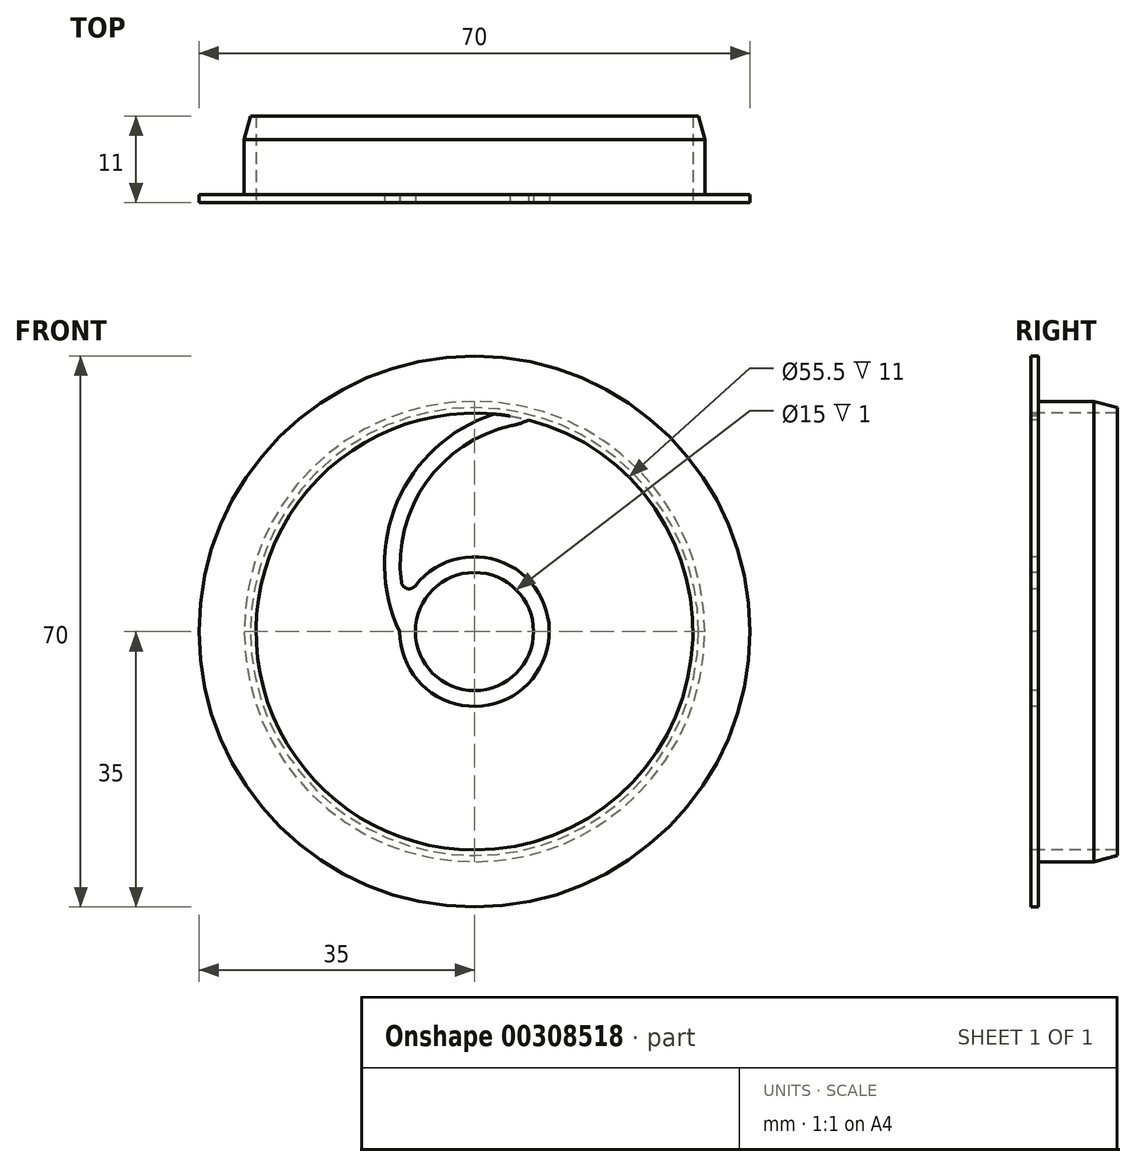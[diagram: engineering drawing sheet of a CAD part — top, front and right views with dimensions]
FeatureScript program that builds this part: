
annotation { "Feature Type Name" : "Feature", "Feature Type Description" : "" }
export const myFeature = defineFeature(function(context is Context, id is Id, definition is map)
    precondition{}
    {
        {
            var Q0;
            Q0=qCreatedBy(makeId("Front.planeOp"),FACE);
            var sketch = newSketch(context, id + "F0", { "sketchPlane" : qUnion([Q0])});
            skCircle(sketch, "E0", {"center": v(0, 0) * mm, "radius": 27.75 * mm});
            skCircle(sketch, "E1.0", {"center": v(0, 0) * mm, "radius": 29.25 * mm});
            skSolve(sketch);
        }
        {
            var Q0;
            Q0 = qSketchRegion(id + "F0", true);
            extrude(context, id + "F1", {"entities" : qUnion([Q0]), "oppositeDirection" : true, "depth" : 10 * mm});
        }
        {
            var Q0;
            Q0=makeQuery(id+"F1.opExtrude","CAP_FACE",FACE,{"disambiguationData":[OSD([sQuery(id+"F0.wireOp",EDGE,"E0"),sQuery(id+"F0.wireOp",EDGE,"E1.0")])],"isStart":true});
            var sketch = newSketch(context, id + "F2", { "sketchPlane" : qUnion([Q0])});
            skCircle(sketch, "E2.0", {"center": v(0, 0) * mm, "radius": 27.75 * mm});
            skCircle(sketch, "E3", {"center": v(0, 0) * mm, "radius": 35 * mm});
            skSolve(sketch);
        }
        {
            var Q0;
            Q0 = qSketchRegion(id + "F2", true);
            extrude(context, id + "F3", {"entities" : qUnion([Q0]), "operationType" : NewBodyOperationType.ADD, "depth" : 1 * mm});
        }
        {
            var Q0;
            Q0=makeQuery(id+"F3.opExtrude","CAP_FACE",FACE,{"disambiguationData":[OSD([sQuery(id+"F2.wireOp",EDGE,"E2.0"),sQuery(id+"F2.wireOp",EDGE,"E3")])],"isStart":false});
            var sketch = newSketch(context, id + "F4", { "sketchPlane" : qUnion([Q0])});
            skCircle(sketch, "E4", {"center": v(0, 0) * mm, "radius": 7.5 * mm});
            skCircle(sketch, "E5.0", {"center": v(0, 0) * mm, "radius": 9.5 * mm});
            skSolve(sketch);
        }
        {
            var Q0;
            Q0 = qSketchRegion(id + "F4", true);
            extrude(context, id + "F5", {"entities" : qUnion([Q0]), "oppositeDirection" : true, "depth" : 1 * mm});
        }
        {
            var Q0;
            Q0=makeQuery(id+"F3.opExtrude","CAP_FACE",FACE,{"disambiguationData":[OSD([sQuery(id+"F2.wireOp",EDGE,"E2.0"),sQuery(id+"F2.wireOp",EDGE,"E3")])],"isStart":false});
            var sketch = newSketch(context, id + "F6", { "sketchPlane" : qUnion([Q0])});
            skArc(sketch, "E6", {"start": v(2.52, 27.63) * mm, "mid": v(-9.77, 16.55) * mm, "end": v(-9.5, 0) * mm});
            skLineSegment(sketch, "E7", {"start": v(-9.5, 0) * mm, "end": v(0, 0) * mm, "construction": true});
            skArc(sketch, "E8.0", {"start": v(8.03, 26.56) * mm, "mid": v(-6.44, 18.5) * mm, "end": v(-8.2, 2.02) * mm});
            skArc(sketch, "E9.0", {"start": v(8.03, 26.56) * mm, "mid": v(5.3, 27.24) * mm, "end": v(2.52, 27.63) * mm});
            skLineSegment(sketch, "E10", {"start": v(-9.5, 0) * mm, "end": v(-8.2, 2.02) * mm});
            skLineSegment(sketch, "E11", {"start": v(0, 0) * mm, "end": v(8.57, 8.57) * mm, "construction": true});
            skSolve(sketch);
        }
        {
            var Q0;
            Q0 = qSketchRegion(id + "F6", true);
            extrude(context, id + "F7", {"entities" : qUnion([Q0]), "operationType" : NewBodyOperationType.ADD, "oppositeDirection" : true, "depth" : 1 * mm});
        }
        {
            var Q0;
            Q0=makeQuery(id+"F7.boolean.opBoolean","INTERSECT",EDGE,{"derivedFrom":[makeQuery(id+"F5.opExtrude","SWEPT_FACE",FACE,{"disambiguationData":[OSD([sQuery(id+"F4.wireOp",EDGE,"E5.0")])]}),makeQuery(id+"F7.opExtrude","SWEPT_FACE",FACE,{"disambiguationData":[OSD([sQuery(id+"F6.wireOp",EDGE,"E8.0")])]})]});
            var Q1;
            Q1=makeQuery(id+"F7.opExtrude","SWEPT_EDGE",EDGE,{"disambiguationData":[OSD([sQuery(id+"F2.wireOp",EDGE,"E2.0"),sQuery(id+"F6.wireOp",EDGE,"E6"),sQuery(id+"F6.wireOp",EDGE,"E9.0")])]});
            fillet(context, id + "F8", {"entities" : qUnion([Q0, Q1]), "radius" : 1 * mm, "tangentPropagation" : true, "allowEdgeOverflow" : false});
        }
        {
            var Q0;
            Q0=makeQuery(id+"F7.opExtrude","SWEPT_EDGE",EDGE,{"disambiguationData":[OSD([sQuery(id+"F6.wireOp",EDGE,"E6"),sQuery(id+"F6.wireOp",EDGE,"E10")])]});
            var Q1;
            Q1=makeQuery(id+"F7.opExtrude","SWEPT_EDGE",EDGE,{"disambiguationData":[OSD([sQuery(id+"F2.wireOp",EDGE,"E2.0"),sQuery(id+"F6.wireOp",EDGE,"E8.0"),sQuery(id+"F6.wireOp",EDGE,"E9.0")])]});
            fillet(context, id + "F9", {"entities" : qUnion([Q0, Q1]), "radius" : 10 * mm, "tangentPropagation" : true, "allowEdgeOverflow" : false});
        }
        {
            var Q0;
            Q0=makeQuery(id+"F1.opExtrude","CAP_EDGE",EDGE,{"disambiguationData":[OSD([sQuery(id+"F0.wireOp",EDGE,"E1.0")])],"isStart":false});
            chamfer(context, id + "F10", {"entities" : qUnion([Q0]), "chamferType" : ChamferType.OFFSET_ANGLE, "width" : 3 * mm, "oppositeDirection" : false, "angle" : 15 * degree, "tangentPropagation" : true});
        }
    });
